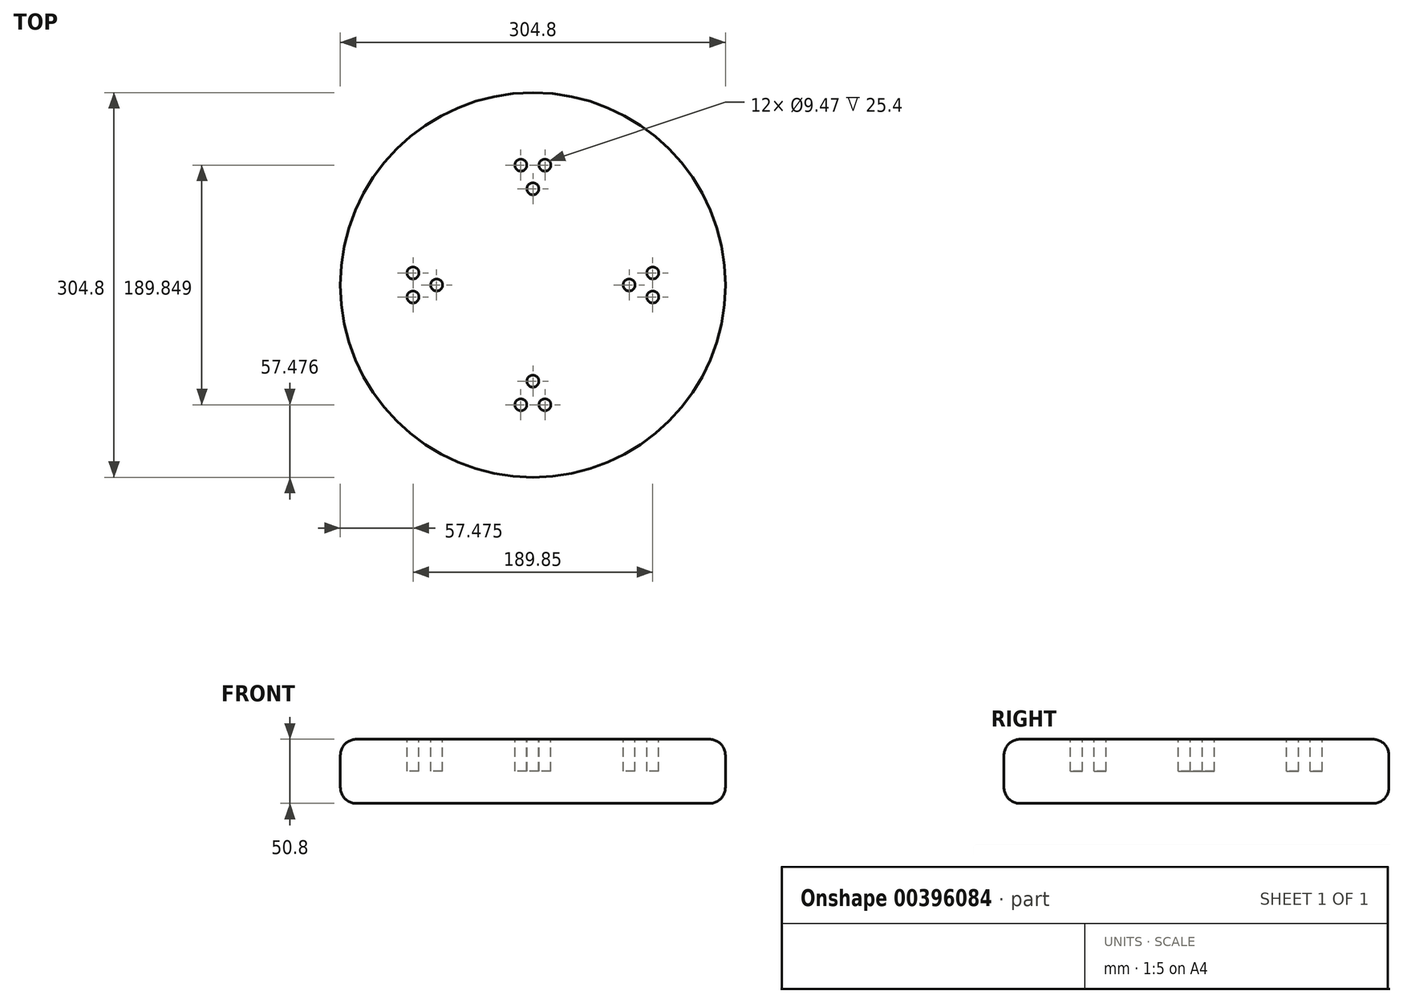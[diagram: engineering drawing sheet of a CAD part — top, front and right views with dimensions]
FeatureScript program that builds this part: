
annotation { "Feature Type Name" : "Feature", "Feature Type Description" : "" }
export const myFeature = defineFeature(function(context is Context, id is Id, definition is map)
    precondition{}
    {
        {
            var Q0;
            Q0=qCreatedBy(makeId("Top.planeOp"),FACE);
            var sketch = newSketch(context, id + "F0", { "sketchPlane" : qUnion([Q0])});
            skCircle(sketch, "E0", {"center": v(0, 0) * mm, "radius": 152.4 * mm});
            skSolve(sketch);
        }
        {
            var Q0;
            Q0=makeQuery(id+"F0.imprint","IMPRINT",FACE,{"disambiguationData":[TD([[makeQuery(id+"F0.imprint","IMPRINT",EDGE,{"derivedFrom":sQuery(id+"F0.wireOp",EDGE,"E0")}),1.0]])]});
            extrude(context, id + "F1", {"entities" : qUnion([Q0]), "depth" : 50.8 * mm});
        }
        {
            var Q0;
            Q0=makeQuery(id+"F1.opExtrude","CAP_EDGE",EDGE,{"disambiguationData":[OSD([sQuery(id+"F0.wireOp",EDGE,"E0")])],"isStart":false});
            var Q1;
            Q1=makeQuery(id+"F1.opExtrude","CAP_EDGE",EDGE,{"disambiguationData":[OSD([sQuery(id+"F0.wireOp",EDGE,"E0")])],"isStart":true});
            fillet(context, id + "F2", {"entities" : qUnion([Q0, Q1]), "radius" : 12.7 * mm, "tangentPropagation" : true, "allowEdgeOverflow" : false});
        }
        {
            var Q0;
            Q0=makeQuery(id+"F1.opExtrude","CAP_FACE",FACE,{"disambiguationData":[OSD([sQuery(id+"F0.wireOp",EDGE,"E0")])],"isStart":false});
            var sketch = newSketch(context, id + "F3", { "sketchPlane" : qUnion([Q0])});
            skCircle(sketch, "E1", {"center": v(0, -76.2) * mm, "radius": 4.73 * mm});
            skPoint(sketch, "E2.middle", {"position": v(0, -82.13) * mm});
            skCircle(sketch, "E3", {"center": v(-9.54, -94.92) * mm, "radius": 4.73 * mm});
            skCircle(sketch, "E4", {"center": v(9.54, -94.92) * mm, "radius": 4.73 * mm});
            skCircle(sketch, "E5", {"center": v(-76.2, 0) * mm, "radius": 4.73 * mm});
            skCircle(sketch, "E6", {"center": v(-94.92, 9.52) * mm, "radius": 4.73 * mm});
            skCircle(sketch, "E7", {"center": v(-94.92, -9.53) * mm, "radius": 4.73 * mm});
            skCircle(sketch, "E8", {"center": v(76.2, 0) * mm, "radius": 4.73 * mm});
            skCircle(sketch, "E9", {"center": v(94.92, -9.52) * mm, "radius": 4.73 * mm});
            skCircle(sketch, "E10", {"center": v(94.92, 9.53) * mm, "radius": 4.73 * mm});
            skCircle(sketch, "E11", {"center": v(0, 76.2) * mm, "radius": 4.73 * mm});
            skCircle(sketch, "E12", {"center": v(9.53, 94.92) * mm, "radius": 4.73 * mm});
            skCircle(sketch, "E13", {"center": v(-9.52, 94.92) * mm, "radius": 4.73 * mm});
            skSolve(sketch);
        }
        {
            var Q0;
            Q0=makeQuery(id+"F3.imprint","IMPRINT",FACE,{"disambiguationData":[TD([[makeQuery(id+"F3.imprint","IMPRINT",EDGE,{"derivedFrom":sQuery(id+"F3.wireOp",EDGE,"E7")}),1.0]])]});
            var Q1;
            Q1=makeQuery(id+"F3.imprint","IMPRINT",FACE,{"disambiguationData":[TD([[makeQuery(id+"F3.imprint","IMPRINT",EDGE,{"derivedFrom":sQuery(id+"F3.wireOp",EDGE,"E6")}),1.0]])]});
            var Q2;
            Q2=makeQuery(id+"F3.imprint","IMPRINT",FACE,{"disambiguationData":[TD([[makeQuery(id+"F3.imprint","IMPRINT",EDGE,{"derivedFrom":sQuery(id+"F3.wireOp",EDGE,"E5")}),1.0]])]});
            var Q3;
            Q3=makeQuery(id+"F3.imprint","IMPRINT",FACE,{"disambiguationData":[TD([[makeQuery(id+"F3.imprint","IMPRINT",EDGE,{"derivedFrom":sQuery(id+"F3.wireOp",EDGE,"E3")}),1.0]])]});
            var Q4;
            Q4=makeQuery(id+"F3.imprint","IMPRINT",FACE,{"disambiguationData":[TD([[makeQuery(id+"F3.imprint","IMPRINT",EDGE,{"derivedFrom":sQuery(id+"F3.wireOp",EDGE,"E1")}),1.0]])]});
            var Q5;
            Q5=makeQuery(id+"F3.imprint","IMPRINT",FACE,{"disambiguationData":[TD([[makeQuery(id+"F3.imprint","IMPRINT",EDGE,{"derivedFrom":sQuery(id+"F3.wireOp",EDGE,"E4")}),1.0]])]});
            var Q6;
            Q6=makeQuery(id+"F3.imprint","IMPRINT",FACE,{"disambiguationData":[TD([[makeQuery(id+"F3.imprint","IMPRINT",EDGE,{"derivedFrom":sQuery(id+"F3.wireOp",EDGE,"E8")}),1.0]])]});
            var Q7;
            Q7=makeQuery(id+"F3.imprint","IMPRINT",FACE,{"disambiguationData":[TD([[makeQuery(id+"F3.imprint","IMPRINT",EDGE,{"derivedFrom":sQuery(id+"F3.wireOp",EDGE,"E10")}),1.0]])]});
            var Q8;
            Q8=makeQuery(id+"F3.imprint","IMPRINT",FACE,{"disambiguationData":[TD([[makeQuery(id+"F3.imprint","IMPRINT",EDGE,{"derivedFrom":sQuery(id+"F3.wireOp",EDGE,"E9")}),1.0]])]});
            var Q9;
            Q9=makeQuery(id+"F3.imprint","IMPRINT",FACE,{"disambiguationData":[TD([[makeQuery(id+"F3.imprint","IMPRINT",EDGE,{"derivedFrom":sQuery(id+"F3.wireOp",EDGE,"E11")}),1.0]])]});
            var Q10;
            Q10=makeQuery(id+"F3.imprint","IMPRINT",FACE,{"disambiguationData":[TD([[makeQuery(id+"F3.imprint","IMPRINT",EDGE,{"derivedFrom":sQuery(id+"F3.wireOp",EDGE,"E12")}),1.0]])]});
            var Q11;
            Q11=makeQuery(id+"F3.imprint","IMPRINT",FACE,{"disambiguationData":[TD([[makeQuery(id+"F3.imprint","IMPRINT",EDGE,{"derivedFrom":sQuery(id+"F3.wireOp",EDGE,"E13")}),1.0]])]});
            var Q12;
            Q12=sQuery(id+"F3.wireOp",EDGE,"E7");
            extrude(context, id + "F4", {"entities" : qUnion([Q0, Q1, Q2, Q3, Q4, Q5, Q6, Q7, Q8, Q9, Q10, Q11]), "operationType" : NewBodyOperationType.REMOVE, "surfaceEntities" : qUnion([Q12]), "oppositeDirection" : true, "depth" : 25.4 * mm});
        }
    });
